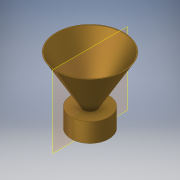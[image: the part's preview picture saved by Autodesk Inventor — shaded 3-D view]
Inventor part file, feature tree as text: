
AUTODESK INVENTOR PART (.ipt)
format: ipt  version: 2019.1 (Build 231200000, 200)  size: 131,072 bytes
history: native  units: mm
features: sketch x2, other x1, extrude x1, revolve x1, projected_geometry x1
ambient origin geometry x8: Origin, YZ Plane, XZ Plane, XY Plane, X Axis, Y Axis, Z Axis, Center Point
bodies: Body1 (feature_tree)
feature tree (6):
  other  "ソリッド1"
  extrude  "押し出し1"  Depth=200.0mm
  revolve  "回転1"
  sketch  "スケッチ1"
  sketch  "スケッチ2"
  projected_geometry  "投影ループ1"
